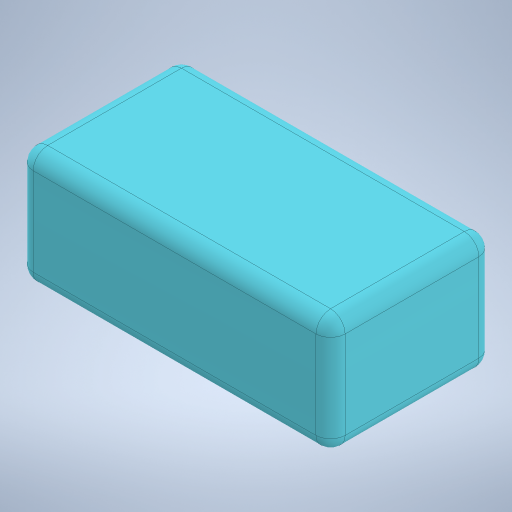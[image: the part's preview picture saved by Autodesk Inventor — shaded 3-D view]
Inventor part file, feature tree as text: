
AUTODESK INVENTOR PART (.ipt)
format: ipt  version: 2024 (Build 280153000, 153)  size: 218,624 bytes
history: native  units: in
note: dims shown in document units (in); Inventor stores cm internally (conversion verified against a paired STEP export)
features: extrude x1, fillet x1, sketch x1
ambient origin geometry x8: Origin, YZ Plane, XZ Plane, XY Plane, X Axis, Y Axis, Z Axis, Center Point
bodies: Solid1 (feature_tree)
feature tree (3):
  extrude  "Extrusion1"  Depth=0.125in
  fillet  "Fillet1"  [1 undecoded]
  sketch  "Sketch1"  dims[d3=0.0in d4=0.125in]
note: 1 required parameter value undecoded (feature->parameter linkage not recoverable at this tier; creation-order binding heuristic only, values carry confidence <= 0.55)
